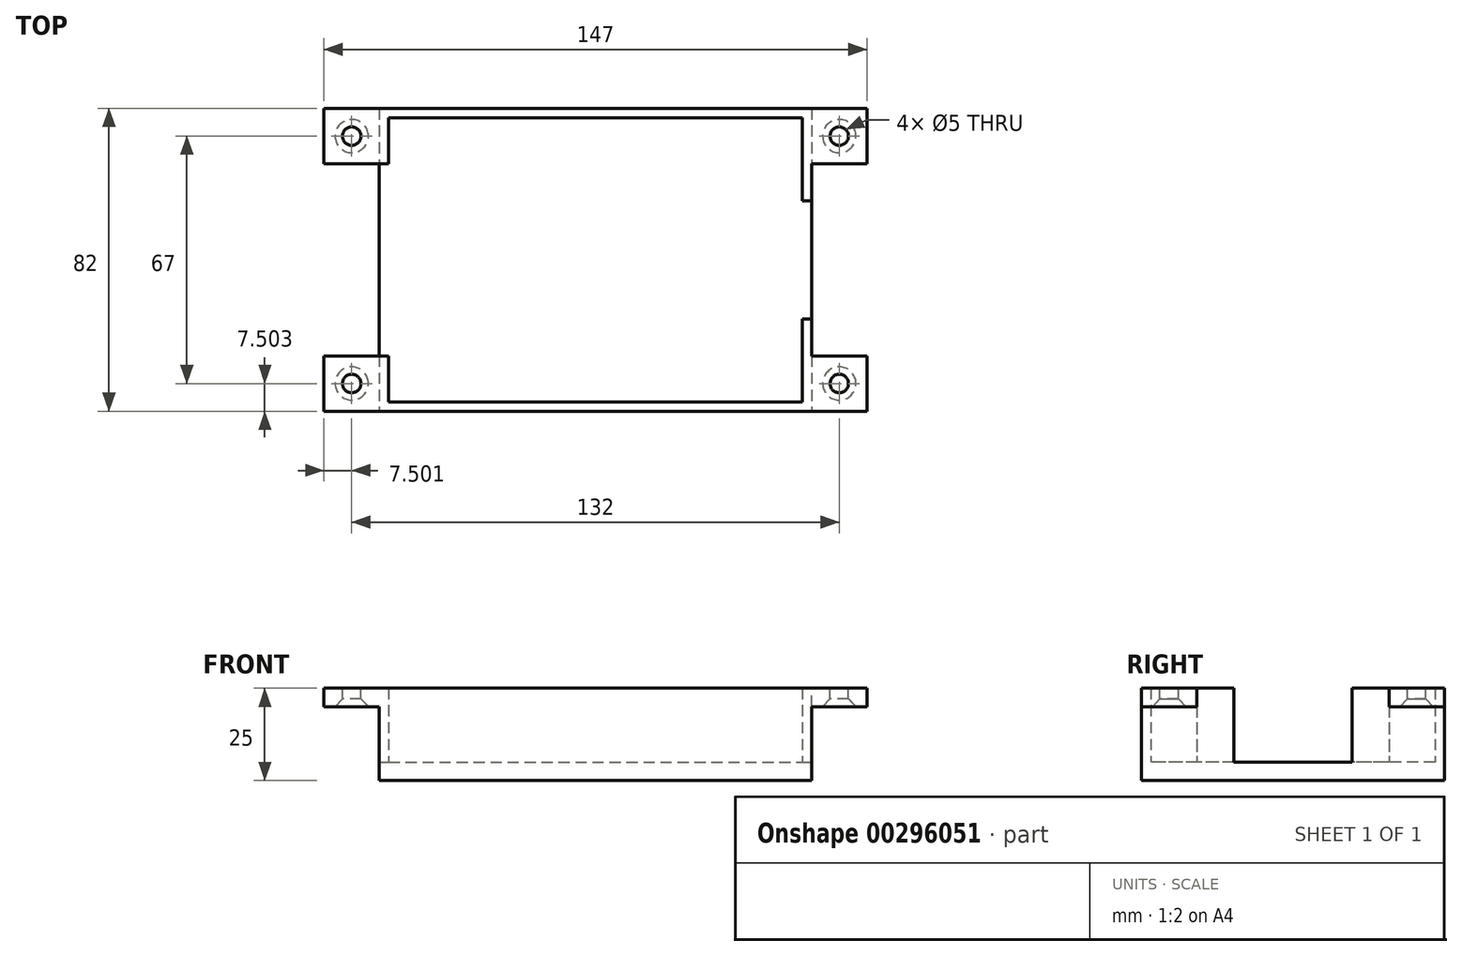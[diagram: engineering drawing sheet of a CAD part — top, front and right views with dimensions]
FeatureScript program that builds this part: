
annotation { "Feature Type Name" : "Feature", "Feature Type Description" : "" }
export const myFeature = defineFeature(function(context is Context, id is Id, definition is map)
    precondition{}
    {
        {
            var Q0;
            Q0=qCreatedBy(makeId("Top.planeOp"),FACE);
            var sketch = newSketch(context, id + "F0", { "sketchPlane" : qUnion([Q0])});
            skLineSegment(sketch, "E0.bottom", {"start": v(-55.35, 52.67) * mm, "end": v(61.65, 52.67) * mm});
            skLineSegment(sketch, "E0.top", {"start": v(-55.35, -29.33) * mm, "end": v(61.65, -29.33) * mm});
            skLineSegment(sketch, "E0.left", {"start": v(-55.35, 52.67) * mm, "end": v(-55.35, -29.33) * mm});
            skLineSegment(sketch, "E0.right", {"start": v(61.65, 52.67) * mm, "end": v(61.65, -29.33) * mm});
            skLineSegment(sketch, "E1.bottom", {"start": v(-52.85, 50.17) * mm, "end": v(59.15, 50.17) * mm});
            skLineSegment(sketch, "E1.top", {"start": v(-52.85, -26.83) * mm, "end": v(59.15, -26.83) * mm});
            skLineSegment(sketch, "E1.left", {"start": v(-52.85, 50.17) * mm, "end": v(-52.85, -26.83) * mm});
            skLineSegment(sketch, "E1.right", {"start": v(59.15, 50.17) * mm, "end": v(59.15, -26.83) * mm});
            skLineSegment(sketch, "E2", {"start": v(59.15, 27.67) * mm, "end": v(61.65, 27.67) * mm});
            skLineSegment(sketch, "E3", {"start": v(59.15, -4.33) * mm, "end": v(61.65, -4.33) * mm});
            skLineSegment(sketch, "E4", {"start": v(-55.35, 37.67) * mm, "end": v(-52.85, 37.67) * mm});
            skLineSegment(sketch, "E5", {"start": v(-55.35, -14.33) * mm, "end": v(-52.85, -14.33) * mm});
            skSolve(sketch);
        }
        {
            var Q0;
            {var subQ2=sQuery(id+"F0.wireOp",EDGE,"E0.bottom");Q0=makeQuery(id+"F0.imprint","IMPRINT",FACE,{"disambiguationData":[TD([[makeQuery(id+"F0.imprint","IMPRINT",EDGE,{"derivedFrom":subQ2}),-1.0]])]});}
            var Q1;
            {var subQ3=sQuery(id+"F0.wireOp",EDGE,"E1.bottom");Q1=makeQuery(id+"F0.imprint","IMPRINT",FACE,{"disambiguationData":[TD([[makeQuery(id+"F0.imprint","IMPRINT",EDGE,{"derivedFrom":subQ3}),-1.0]])]});}
            var Q2;
            {var subQ0=sQuery(id+"F0.wireOp",EDGE,"E2");Q2=makeQuery(id+"F0.imprint","IMPRINT",FACE,{"disambiguationData":[TD([[makeQuery(id+"F0.imprint","IMPRINT",EDGE,{"derivedFrom":subQ0}),-1.0]])]});}
            var Q3;
            {var subQ1=sQuery(id+"F0.wireOp",EDGE,"E0.top");Q3=makeQuery(id+"F0.imprint","IMPRINT",FACE,{"disambiguationData":[TD([[makeQuery(id+"F0.imprint","IMPRINT",EDGE,{"derivedFrom":subQ1}),1.0]])]});}
            var Q4;
            {var subQ0=sQuery(id+"F0.wireOp",EDGE,"E4");Q4=makeQuery(id+"F0.imprint","IMPRINT",FACE,{"disambiguationData":[TD([[makeQuery(id+"F0.imprint","IMPRINT",EDGE,{"derivedFrom":subQ0}),-1.0]])]});}
            extrude(context, id + "F1", {"entities" : qUnion([Q0, Q1, Q2, Q3, Q4]), "oppositeDirection" : true, "depth" : 5 * mm});
        }
        {
            var Q0;
            {var subQ2=sQuery(id+"F0.wireOp",EDGE,"E0.bottom");Q0=makeQuery(id+"F0.imprint","IMPRINT",FACE,{"disambiguationData":[TD([[makeQuery(id+"F0.imprint","IMPRINT",EDGE,{"derivedFrom":subQ2}),-1.0]])]});}
            var Q1;
            {var subQ1=sQuery(id+"F0.wireOp",EDGE,"E0.top");Q1=makeQuery(id+"F0.imprint","IMPRINT",FACE,{"disambiguationData":[TD([[makeQuery(id+"F0.imprint","IMPRINT",EDGE,{"derivedFrom":subQ1}),1.0]])]});}
            extrude(context, id + "F2", {"entities" : qUnion([Q0, Q1]), "operationType" : NewBodyOperationType.ADD, "depth" : 20 * mm});
        }
        {
            var Q0;
            Q0=makeQuery(id+"F2.opExtrude","CAP_FACE",FACE,{"disambiguationData":[OSD([sQuery(id+"F0.wireOp",EDGE,"E0.bottom"),sQuery(id+"F0.wireOp",EDGE,"E0.left"),sQuery(id+"F0.wireOp",EDGE,"E0.right"),sQuery(id+"F0.wireOp",EDGE,"E1.bottom"),sQuery(id+"F0.wireOp",EDGE,"E1.left"),sQuery(id+"F0.wireOp",EDGE,"E1.right"),sQuery(id+"F0.wireOp",EDGE,"E2"),sQuery(id+"F0.wireOp",EDGE,"E4")])],"isStart":false});
            var sketch = newSketch(context, id + "F3", { "sketchPlane" : qUnion([Q0])});
            skLineSegment(sketch, "E6.bottom", {"start": v(-55.35, 37.67) * mm, "end": v(-70.35, 37.67) * mm});
            skLineSegment(sketch, "E6.top", {"start": v(-55.35, 52.67) * mm, "end": v(-70.35, 52.67) * mm});
            skLineSegment(sketch, "E6.left", {"start": v(-55.35, 37.67) * mm, "end": v(-55.35, 52.67) * mm});
            skLineSegment(sketch, "E6.right", {"start": v(-70.35, 37.67) * mm, "end": v(-70.35, 52.67) * mm});
            skLineSegment(sketch, "E7.bottom", {"start": v(61.65, 37.67) * mm, "end": v(76.65, 37.67) * mm});
            skLineSegment(sketch, "E7.top", {"start": v(61.65, 52.67) * mm, "end": v(76.65, 52.67) * mm});
            skLineSegment(sketch, "E7.left", {"start": v(61.65, 37.67) * mm, "end": v(61.65, 52.67) * mm});
            skLineSegment(sketch, "E7.right", {"start": v(76.65, 37.67) * mm, "end": v(76.65, 52.67) * mm});
            skCircle(sketch, "E8", {"center": v(69.15, 45.17) * mm, "radius": 2.5 * mm});
            skCircle(sketch, "E9", {"center": v(-62.85, 45.17) * mm, "radius": 2.5 * mm});
            skSolve(sketch);
        }
        {
            var Q0;
            Q0=makeQuery(id+"F2.opExtrude","CAP_FACE",FACE,{"disambiguationData":[OSD([sQuery(id+"F0.wireOp",EDGE,"E0.top"),sQuery(id+"F0.wireOp",EDGE,"E0.left"),sQuery(id+"F0.wireOp",EDGE,"E0.right"),sQuery(id+"F0.wireOp",EDGE,"E1.top"),sQuery(id+"F0.wireOp",EDGE,"E1.left"),sQuery(id+"F0.wireOp",EDGE,"E1.right"),sQuery(id+"F0.wireOp",EDGE,"E3"),sQuery(id+"F0.wireOp",EDGE,"E5")])],"isStart":false});
            var sketch = newSketch(context, id + "F4", { "sketchPlane" : qUnion([Q0])});
            skLineSegment(sketch, "E10.bottom", {"start": v(61.65, -29.33) * mm, "end": v(76.65, -29.33) * mm});
            skLineSegment(sketch, "E10.top", {"start": v(61.65, -14.33) * mm, "end": v(76.65, -14.33) * mm});
            skLineSegment(sketch, "E10.left", {"start": v(61.65, -29.33) * mm, "end": v(61.65, -14.33) * mm});
            skLineSegment(sketch, "E10.right", {"start": v(76.65, -29.33) * mm, "end": v(76.65, -14.33) * mm});
            skLineSegment(sketch, "E11.bottom", {"start": v(-55.35, -29.33) * mm, "end": v(-70.35, -29.33) * mm});
            skLineSegment(sketch, "E11.top", {"start": v(-55.35, -14.33) * mm, "end": v(-70.35, -14.33) * mm});
            skLineSegment(sketch, "E11.left", {"start": v(-55.35, -29.33) * mm, "end": v(-55.35, -14.33) * mm});
            skLineSegment(sketch, "E11.right", {"start": v(-70.35, -29.33) * mm, "end": v(-70.35, -14.33) * mm});
            skCircle(sketch, "E12", {"center": v(-62.85, -21.83) * mm, "radius": 2.5 * mm});
            skCircle(sketch, "E13", {"center": v(69.15, -21.83) * mm, "radius": 2.5 * mm});
            skSolve(sketch);
        }
        {
            var Q0;
            Q0=makeQuery(id+"F3.imprint","IMPRINT",FACE,{"disambiguationData":[TD([[makeQuery(id+"F3.imprint","IMPRINT",EDGE,{"derivedFrom":sQuery(id+"F3.wireOp",EDGE,"E6.bottom")}),-1.0]])]});
            var Q1;
            Q1=makeQuery(id+"F4.imprint","IMPRINT",FACE,{"disambiguationData":[TD([[makeQuery(id+"F4.imprint","IMPRINT",EDGE,{"derivedFrom":sQuery(id+"F4.wireOp",EDGE,"E11.bottom")}),-1.0]])]});
            var Q2;
            Q2=makeQuery(id+"F3.imprint","IMPRINT",FACE,{"disambiguationData":[TD([[makeQuery(id+"F3.imprint","IMPRINT",EDGE,{"derivedFrom":sQuery(id+"F3.wireOp",EDGE,"E7.bottom")}),1.0]])]});
            var Q3;
            Q3=makeQuery(id+"F4.imprint","IMPRINT",FACE,{"disambiguationData":[TD([[makeQuery(id+"F4.imprint","IMPRINT",EDGE,{"derivedFrom":sQuery(id+"F4.wireOp",EDGE,"E10.bottom")}),1.0]])]});
            extrude(context, id + "F5", {"entities" : qUnion([Q0, Q1, Q2, Q3]), "operationType" : NewBodyOperationType.ADD, "oppositeDirection" : true, "depth" : 5 * mm});
        }
        {
            var Q0;
            Q0=makeQuery(id+"F5.opExtrude","CAP_EDGE",EDGE,{"disambiguationData":[OSD([sQuery(id+"F4.wireOp",EDGE,"E13")])],"isStart":false});
            chamfer(context, id + "F6", {"entities" : qUnion([Q0]), "chamferType" : ChamferType.OFFSET_ANGLE, "width" : 2 * mm, "oppositeDirection" : false, "angle" : 47 * degree, "tangentPropagation" : true});
        }
        {
            var Q0;
            Q0=makeQuery(id+"F5.opExtrude","CAP_EDGE",EDGE,{"disambiguationData":[OSD([sQuery(id+"F3.wireOp",EDGE,"E8")])],"isStart":false});
            chamfer(context, id + "F7", {"entities" : qUnion([Q0]), "chamferType" : ChamferType.OFFSET_ANGLE, "width" : 2 * mm, "oppositeDirection" : false, "angle" : 47 * degree, "tangentPropagation" : true});
        }
        {
            var Q0;
            Q0=makeQuery(id+"F5.opExtrude","CAP_EDGE",EDGE,{"disambiguationData":[OSD([sQuery(id+"F4.wireOp",EDGE,"E12")])],"isStart":false});
            var Q1;
            Q1=makeQuery(id+"F5.opExtrude","CAP_EDGE",EDGE,{"disambiguationData":[OSD([sQuery(id+"F3.wireOp",EDGE,"E9")])],"isStart":false});
            chamfer(context, id + "F8", {"entities" : qUnion([Q0, Q1]), "chamferType" : ChamferType.OFFSET_ANGLE, "width" : 2 * mm, "oppositeDirection" : false, "angle" : 47 * degree, "tangentPropagation" : true});
        }
    });
